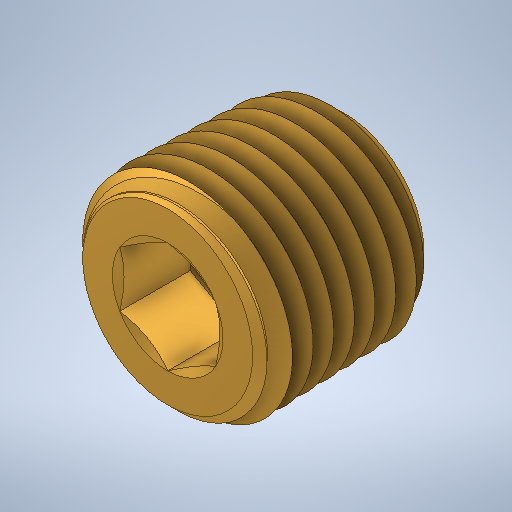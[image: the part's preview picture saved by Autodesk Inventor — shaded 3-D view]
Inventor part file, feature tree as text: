
AUTODESK INVENTOR PART (.ipt)
format: ipt  version: 2025 (Build 290162000, 162)  size: 552,448 bytes
history: native  units: mm
features: extrude x1
ambient origin geometry x8: Origin, YZ Plane, XZ Plane, XY Plane, X Axis, Y Axis, Z Axis, Center Point
bodies: Solid1 (feature_tree)
feature tree (1):
  extrude  "Extrude5"  [1 undecoded]
note: 1 required parameter value undecoded (feature->parameter linkage not recoverable at this tier; creation-order binding heuristic only, values carry confidence <= 0.55)
